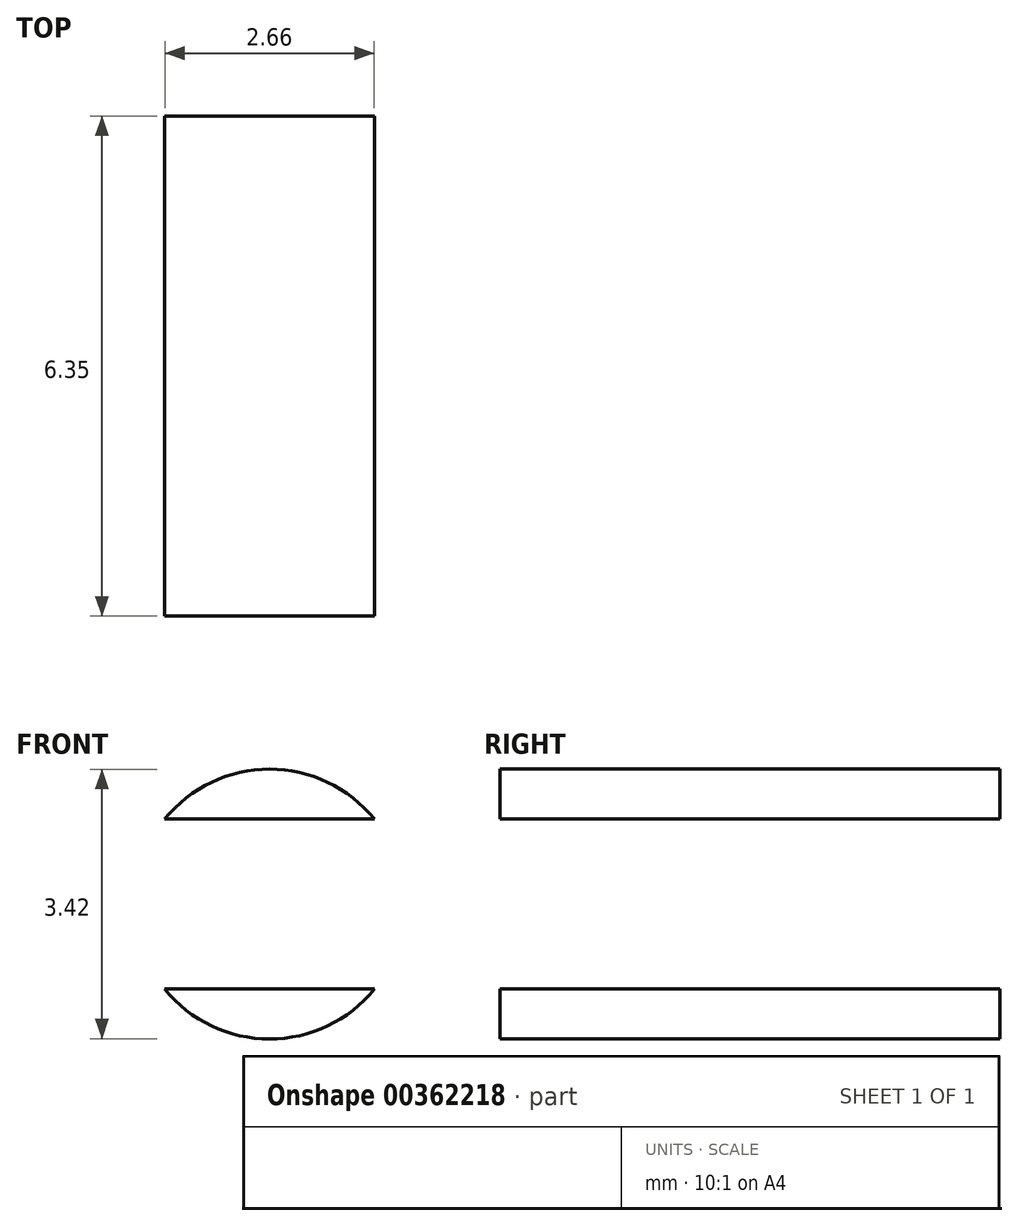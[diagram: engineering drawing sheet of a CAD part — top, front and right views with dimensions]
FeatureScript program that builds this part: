
annotation { "Feature Type Name" : "Feature", "Feature Type Description" : "" }
export const myFeature = defineFeature(function(context is Context, id is Id, definition is map)
    precondition{}
    {
        {
            var Q0;
            Q0=qCreatedBy(makeId("Front.planeOp"),FACE);
            var sketch = newSketch(context, id + "F0", { "sketchPlane" : qUnion([Q0])});
            skPoint(sketch, "E0.middle", {"position": v(0, 0) * mm});
            skCircle(sketch, "E1", {"center": v(0, 0) * mm, "radius": 1.71 * mm});
            skLineSegment(sketch, "E2", {"start": v(-1.33, 1.08) * mm, "end": v(1.33, 1.08) * mm});
            skLineSegment(sketch, "E3", {"start": v(-1.33, -1.08) * mm, "end": v(1.33, -1.08) * mm});
            skCircle(sketch, "E4", {"center": v(0, 0) * mm, "radius": 12.58 * mm});
            skSolve(sketch);
        }
        {
            var Q0;
            Q0=makeQuery(id+"F0.imprint","IMPRINT",FACE,{"disambiguationData":[TD([[makeQuery(id+"F0.imprint","IMPRINT",EDGE,{"derivedFrom":sQuery(id+"F0.wireOp",EDGE,"E0.bottom")}),1.0]])]});
            var Q1;
            Q1=makeQuery(id+"F0.imprint","IMPRINT",FACE,{"disambiguationData":[TD([[makeQuery(id+"F0.imprint","IMPRINT",EDGE,{"derivedFrom":sQuery(id+"F0.wireOp",EDGE,"E0.right")}),-1.0]])]});
            var Q2;
            {var subQ0=sQuery(id+"F0.wireOp",EDGE,"E2");Q2=makeQuery(id+"F0.imprint","IMPRINT",FACE,{"disambiguationData":[TD([[makeQuery(id+"F0.imprint","IMPRINT",EDGE,{"derivedFrom":subQ0}),1.0]])]});}
            var Q3;
            Q3=makeQuery(id+"F0.imprint","IMPRINT",FACE,{"disambiguationData":[TD([[makeQuery(id+"F0.imprint","IMPRINT",EDGE,{"derivedFrom":sQuery(id+"F0.wireOp",EDGE,"E0.left")}),1.0]])]});
            var Q4;
            {var subQ0=sQuery(id+"F0.wireOp",EDGE,"E3");Q4=makeQuery(id+"F0.imprint","IMPRINT",FACE,{"disambiguationData":[TD([[makeQuery(id+"F0.imprint","IMPRINT",EDGE,{"derivedFrom":subQ0}),-1.0]])]});}
            extrude(context, id + "F1", {"entities" : qUnion([Q0, Q1, Q2, Q3, Q4]), "depth" : 6.35 * mm});
        }
    });
